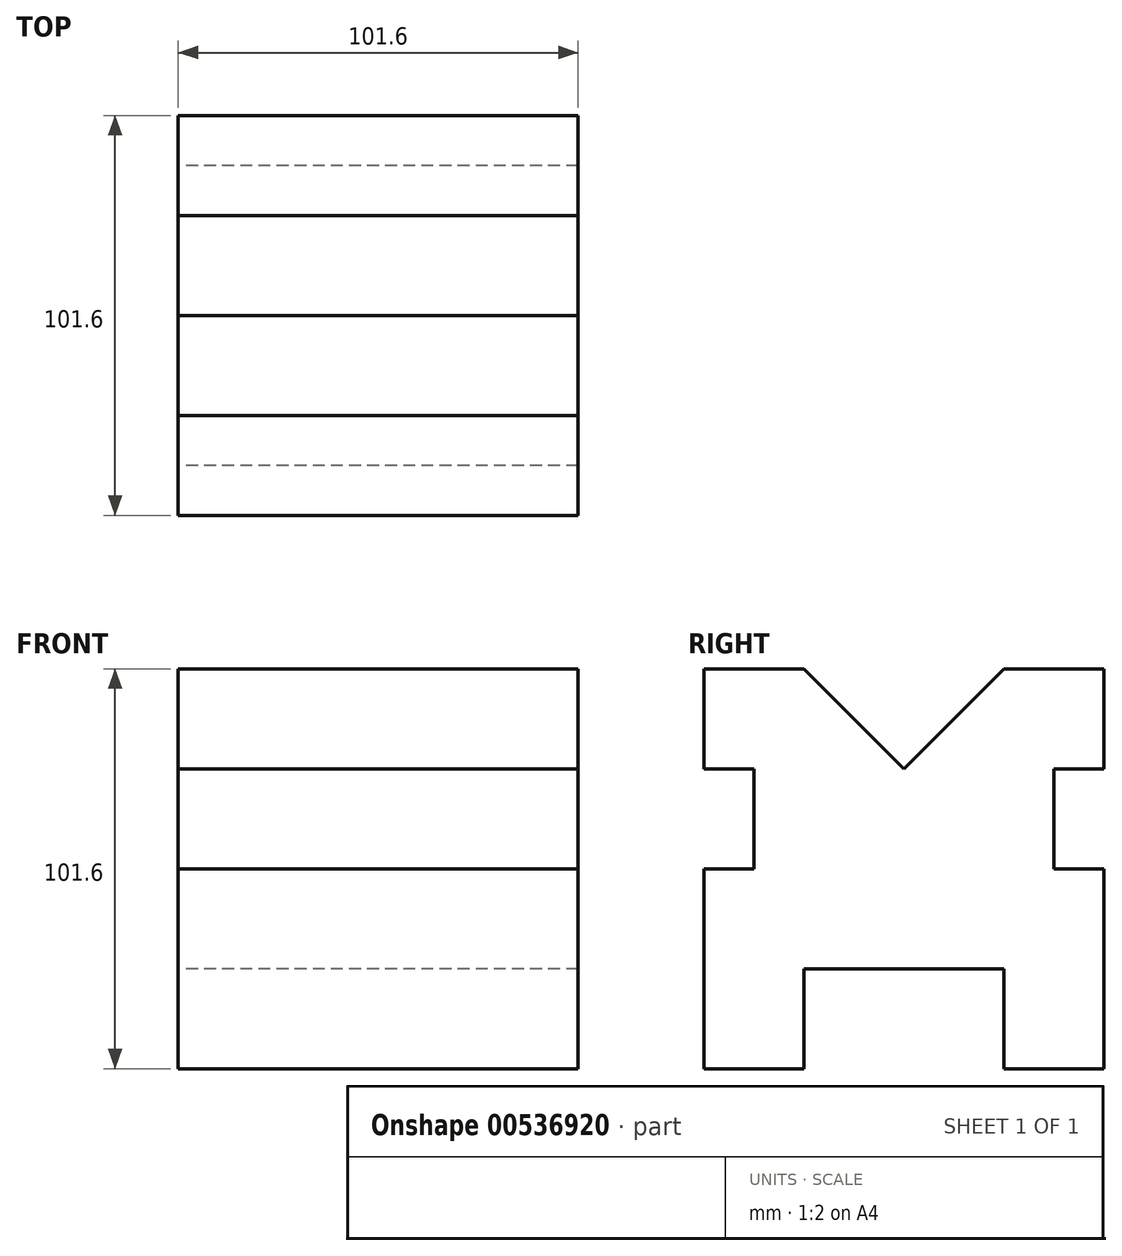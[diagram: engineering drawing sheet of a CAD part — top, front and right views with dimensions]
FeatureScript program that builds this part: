
annotation { "Feature Type Name" : "Feature", "Feature Type Description" : "" }
export const myFeature = defineFeature(function(context is Context, id is Id, definition is map)
    precondition{}
    {
        {
            var Q0;
            Q0=qCreatedBy(makeId("Right.planeOp"),FACE);
            var sketch = newSketch(context, id + "F0", { "sketchPlane" : qUnion([Q0])});
            skLineSegment(sketch, "E0", {"start": v(0, 0) * mm, "end": v(-25.4, 0) * mm});
            skLineSegment(sketch, "E1", {"start": v(-25.4, 0) * mm, "end": v(-25.4, 25.4) * mm});
            skLineSegment(sketch, "E2", {"start": v(-25.4, 25.4) * mm, "end": v(-76.2, 25.4) * mm});
            skLineSegment(sketch, "E3", {"start": v(-76.2, 25.4) * mm, "end": v(-76.2, 0) * mm});
            skLineSegment(sketch, "E4", {"start": v(-76.2, 0) * mm, "end": v(-101.6, 0) * mm});
            skLineSegment(sketch, "E5", {"start": v(-101.6, 0) * mm, "end": v(-101.6, 50.8) * mm});
            skLineSegment(sketch, "E6", {"start": v(-101.6, 50.8) * mm, "end": v(-88.9, 50.8) * mm});
            skLineSegment(sketch, "E7", {"start": v(-88.9, 50.8) * mm, "end": v(-88.9, 76.2) * mm});
            skLineSegment(sketch, "E8", {"start": v(-88.9, 76.2) * mm, "end": v(-101.6, 76.2) * mm});
            skLineSegment(sketch, "E9", {"start": v(-101.6, 76.2) * mm, "end": v(-101.6, 101.6) * mm});
            skLineSegment(sketch, "E10", {"start": v(-101.6, 101.6) * mm, "end": v(-76.2, 101.6) * mm});
            skLineSegment(sketch, "E11", {"start": v(0, 0) * mm, "end": v(0, 50.8) * mm});
            skLineSegment(sketch, "E12", {"start": v(0, 50.8) * mm, "end": v(-12.7, 50.8) * mm});
            skLineSegment(sketch, "E13", {"start": v(-12.7, 50.8) * mm, "end": v(-12.7, 76.2) * mm});
            skLineSegment(sketch, "E14", {"start": v(-12.7, 76.2) * mm, "end": v(0, 76.2) * mm});
            skLineSegment(sketch, "E15", {"start": v(0, 76.2) * mm, "end": v(0, 101.6) * mm});
            skLineSegment(sketch, "E16", {"start": v(0, 101.6) * mm, "end": v(-25.4, 101.6) * mm});
            skLineSegment(sketch, "E17", {"start": v(-25.4, 25.4) * mm, "end": v(-50.8, 25.4) * mm});
            skLineSegment(sketch, "E18", {"start": v(-25.4, 101.6) * mm, "end": v(-50.8, 76.2) * mm});
            skLineSegment(sketch, "E19", {"start": v(-50.8, 76.2) * mm, "end": v(-76.2, 101.6) * mm});
            skSolve(sketch);
        }
        {
            var Q0;
            Q0 = qSketchRegion(id + "F0", true);
            extrude(context, id + "F1", {"entities" : qUnion([Q0]), "depth" : 101.6 * mm, "offsetDistance" : 25.4 * mm});
        }
    });
